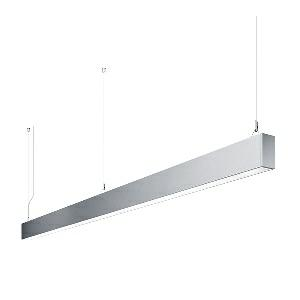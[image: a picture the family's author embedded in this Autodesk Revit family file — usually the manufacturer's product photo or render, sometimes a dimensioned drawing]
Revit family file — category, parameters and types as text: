
# Revit family: dotoo_line_-_dlp_3000_830_d_00805851_2a1d
name_source: partatom
category: Lighting Fixtures
units: mm (PartAtom-declared; Revit-internal decimal feet)

## family parameters
Cut with Voids When Loaded = No
Host = Face
Light Source = No
Part Type = Normal
Room Calculation Point = No
Round Connector Dimension = Use Diameter
Shared = No

## types (1)
- DOTOO.line - DLP 3000/830/D (1 x LED, 2650 lm, 3000K)
    Apparent Load = 26 VA
    Approval mark = CE
    CIE Flux Codes = 67 91 98 100 100
    Color Rendering = 80-89
    Color Temperature = 3000K
    Control Gear = Electronic ballast
    Default Elevation = 1800 mm
    Description = DLP 3000/830/D|Suspended luminaire|light source: LED|connected load: 220-240 V, 50/60 Hz|Power consumption: approx. 26 W|standby: approx. 0,15|luminous flux: 2650 lm|luminous efficacy: 101 lm/W|light distribution: Direct|direct ratio: approx. 100 %|colour temperature: Warm white, ca. 3000 K|color rendering index (CRI): >= 80|chromaticity tolerance:  3 SDCM|System of protection: IP 40|technology: Continuously dimmable|luminaire body|material: Sectional aluminium|colour: Silver|lamp cover: Acrylic (PMMA), Clear|mains lead: 2.00 m With free stranded wires|Fastening: Steel cable 0.3 - 0.7 m|glare control: Prism aperture|luminance(L65): <= 3000 cd/m|unified glare rating(4H 8H): <=  19|special features: DALI Load 1x, TouchDIM - dimming via standard switch, Flicker-free, Suitable as emergency lighting|
    Frequency = 50 Hz
    Height = 110 mm
    Lamp = 1 x LED
    Lamp Light Flux = 2650 lm
    Lamp count = 1
    Length = 2256 mm
    Luminous efficacy = 102 lm/W
    Manufacturer = Waldmann
    ModVariant = No
    Model = 00805851
    Mounting Place = Ceiling
    Mounting Type = Pendant
    Number of Poles = 1
    OnlyDefault = Yes
    Power Factor = 1
    Product Name = DOTOO.line - DLP 3000/830/D
    Product group = Suspended luminaire
    ProductGroupID = 9
    Protection Class = Protection class I
    Protection Degree = IP 40
    RLX_Detail_Level = 1
    RLX_Emergency_Light_Flux = 0 lm
    RLX_Emergency_Type = 0
    RLX_Emergency_Type_DB = No
    RlxData = <blob elided: 23341 chars, md5=102781bc>
    Socket = socket
    Standby Power = 0 W
    System Light Flux = 2650 lm
    System Power = 26 W
    Type Comments = Product without accessories
    Type Image = 113294000-00692533.jpg
    URL = http://relux.com
    VarID = ---
    Voltage = 230 V
    Voltage Range = 220-240 V
    Weight = 0.00 kg
    Width = 60 mm  [stored 0.19685 ft]

note: [stored X ft] marks values corroborated as IEEE doubles in the binary element streams (Revit-internal decimal feet)

## geometry (parser evidence)
native form markers: Blend x4, Sweep x11
no freeform markers — native parametric forms only
